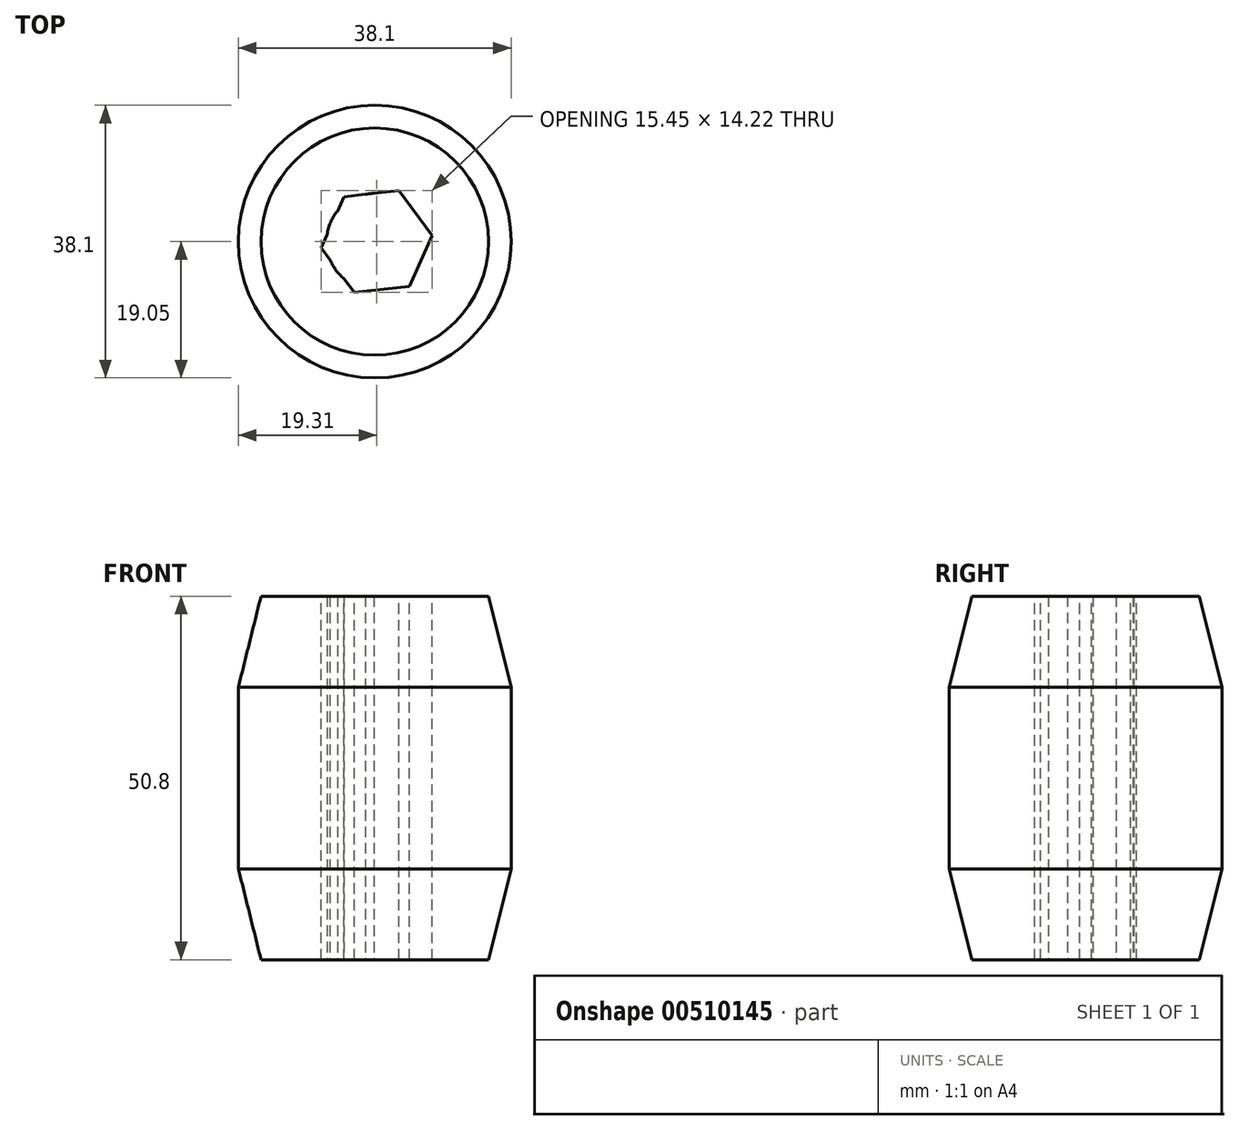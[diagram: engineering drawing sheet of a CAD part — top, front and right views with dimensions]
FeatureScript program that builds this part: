
annotation { "Feature Type Name" : "Feature", "Feature Type Description" : "" }
export const myFeature = defineFeature(function(context is Context, id is Id, definition is map)
    precondition{}
    {
        {
            var Q0;
            Q0=qCreatedBy(makeId("Front.planeOp"),FACE);
            var sketch = newSketch(context, id + "F0", { "sketchPlane" : qUnion([Q0])});
            skLineSegment(sketch, "E0", {"start": v(-0.26, -42.67) * mm, "end": v(-0.26, 42.09) * mm, "construction": true});
            skLineSegment(sketch, "E1", {"start": v(-7, -25.28) * mm, "end": v(-7, 25.52) * mm});
            skLineSegment(sketch, "E2", {"start": v(-19.3, -12.58) * mm, "end": v(-19.3, 12.82) * mm});
            skLineSegment(sketch, "E3", {"start": v(-19.3, -12.58) * mm, "end": v(-16.13, -25.28) * mm});
            skLineSegment(sketch, "E4", {"start": v(-19.3, 12.82) * mm, "end": v(-16.13, 25.52) * mm});
            skLineSegment(sketch, "E5", {"start": v(-16.13, 25.52) * mm, "end": v(-7, 25.52) * mm});
            skLineSegment(sketch, "E6", {"start": v(-16.13, -25.28) * mm, "end": v(-7, -25.28) * mm});
            skSolve(sketch);
        }
        {
            var Q0;
            Q0=qSketchRegion(id+"F0",true);
            var Q1;
            Q1=sQuery(id+"F0.wireOp",EDGE,"E0");
            revolve(context, id + "F1", {"entities" : qUnion([Q0]), "axis" : qUnion([Q1]), "revolveType" : RevolveType.FULL});
        }
        {
            var Q0;
            Q0=qCreatedBy(makeId("Top.planeOp"),FACE);
            var sketch = newSketch(context, id + "F2", { "sketchPlane" : qUnion([Q0])});
            skCircle(sketch, "E7.cCircle", {"center": v(0, 0) * mm, "radius": 6.73 * mm, "construction": true});
            skLineSegment(sketch, "E7.0", {"start": v(3.14, 7.11) * mm, "end": v(7.73, 0.84) * mm});
            skLineSegment(sketch, "E7.1", {"start": v(7.73, 0.84) * mm, "end": v(4.6, -6.27) * mm});
            skLineSegment(sketch, "E7.2", {"start": v(4.6, -6.27) * mm, "end": v(-3.14, -7.11) * mm});
            skLineSegment(sketch, "E7.3", {"start": v(-3.14, -7.11) * mm, "end": v(-7.73, -0.84) * mm});
            skLineSegment(sketch, "E7.4", {"start": v(-7.73, -0.84) * mm, "end": v(-4.6, 6.27) * mm});
            skLineSegment(sketch, "E7.5", {"start": v(-4.6, 6.27) * mm, "end": v(3.14, 7.11) * mm});
            skPoint(sketch, "E7.0.midPoint", {"position": v(5.43, 3.98) * mm});
            skSolve(sketch);
        }
        {
            var Q0;
            Q0=qSketchRegion(id+"F2",true);
            extrude(context, id + "F3", {"entities" : qUnion([Q0]), "operationType" : NewBodyOperationType.REMOVE, "oppositeDirection" : true, "depth" : 50.8 * mm, "hasSecondDirection" : true, "secondDirectionOppositeDirection" : true, "secondDirectionDepth" : -50.8 * mm});
        }
    });
